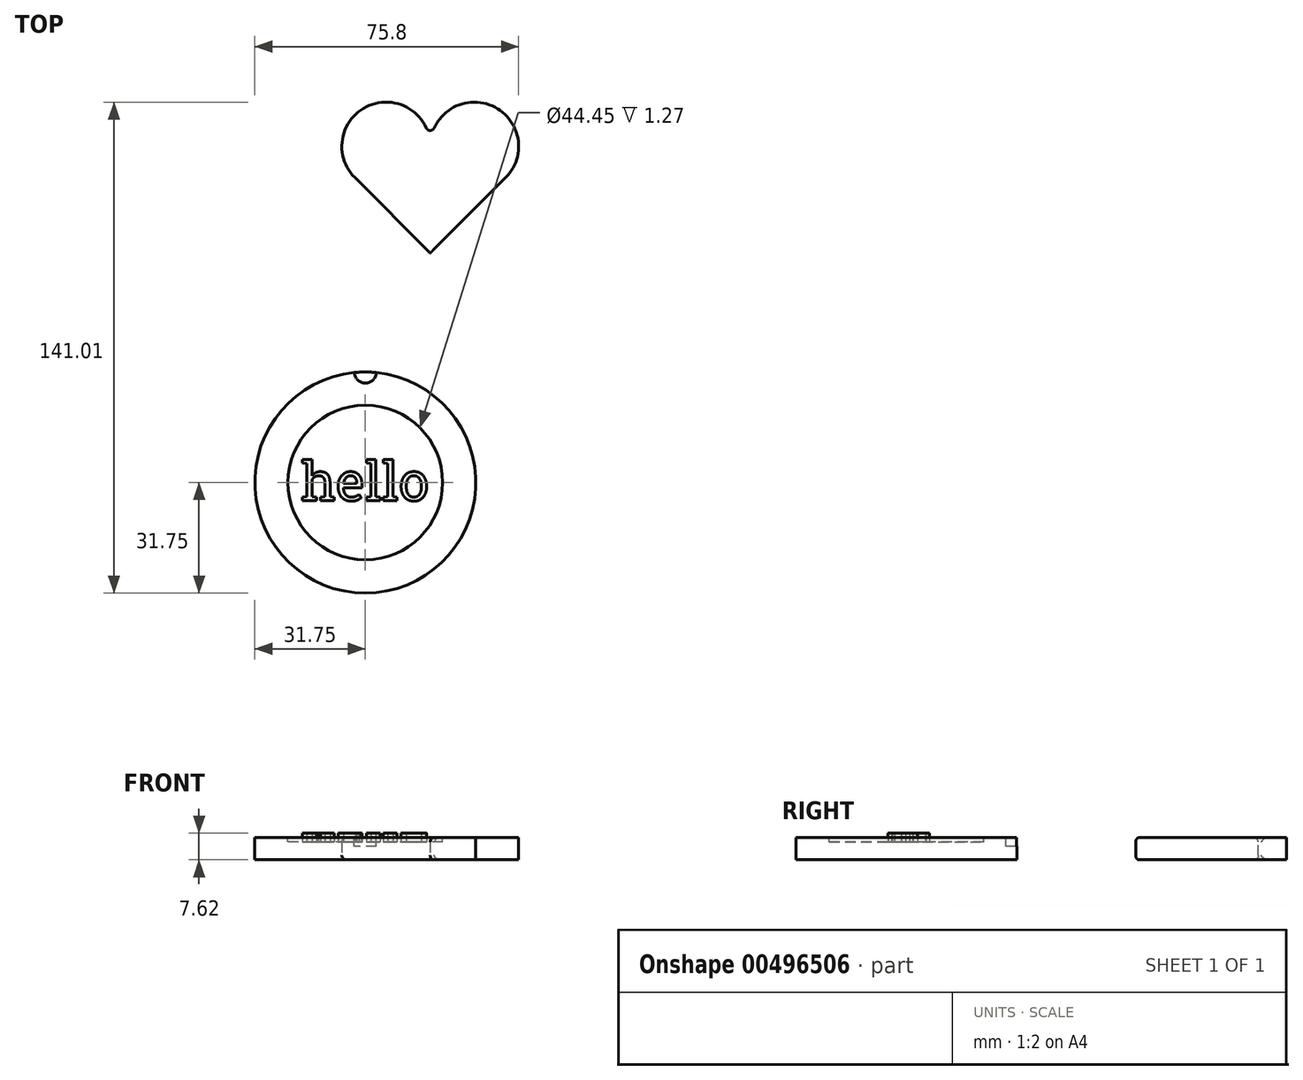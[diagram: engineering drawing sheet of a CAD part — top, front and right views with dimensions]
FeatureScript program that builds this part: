
annotation { "Feature Type Name" : "Feature", "Feature Type Description" : "" }
export const myFeature = defineFeature(function(context is Context, id is Id, definition is map)
    precondition{}
    {
        {
            var Q0;
            Q0=qCreatedBy(makeId("Top.planeOp"),FACE);
            var sketch = newSketch(context, id + "F0", { "sketchPlane" : qUnion([Q0])});
            skCircle(sketch, "E0", {"center": v(0, 0) * mm, "radius": 31.75 * mm});
            skSolve(sketch);
        }
        {
            var Q0;
            Q0 = qSketchRegion(id + "F0", true);
            extrude(context, id + "F1", {"entities" : qUnion([Q0]), "depth" : 6.35 * mm});
        }
        {
            var Q0;
            Q0=makeQuery(id+"F1.opExtrude","CAP_FACE",FACE,{"disambiguationData":[OSD([sQuery(id+"F0.wireOp",EDGE,"E0")])],"isStart":false});
            var sketch = newSketch(context, id + "F2", { "sketchPlane" : qUnion([Q0])});
            skCircle(sketch, "E1", {"center": v(0, 0) * mm, "radius": 22.23 * mm});
            skSolve(sketch);
        }
        {
            var Q0;
            Q0=makeQuery(id+"F2.imprint","IMPRINT",FACE,{"disambiguationData":[TD([[makeQuery(id+"F2.imprint","IMPRINT",EDGE,{"derivedFrom":sQuery(id+"F2.wireOp",EDGE,"E1")}),1.0]])]});
            extrude(context, id + "F3", {"entities" : qUnion([Q0]), "operationType" : NewBodyOperationType.REMOVE, "oppositeDirection" : true, "depth" : 1.27 * mm});
        }
        {
            var Q0;
            Q0=makeQuery(id+"F3.boolean.opBoolean","COPY",FACE,{"derivedFrom":makeQuery(id+"F3.opExtrude","CAP_FACE",FACE,{"disambiguationData":[OSD([sQuery(id+"F2.wireOp",EDGE,"E1")])],"isStart":false})});
            var sketch = newSketch(context, id + "F4", { "sketchPlane" : qUnion([Q0])});
            skText(sketch, "E2", { "text": "hello", "fontName": "RobotoSlab-Regular.ttf"});
            const initialGuessF4  = {"E2": [-0.0185, -0.0052, 1, 0, 0.01116]};
            skSetInitialGuess(sketch, initialGuessF4);
            skSolve(sketch);
        }
        {
            var Q0;
            Q0 = qSketchRegion(id + "F4", true);
            extrude(context, id + "F5", {"entities" : qUnion([Q0]), "operationType" : NewBodyOperationType.ADD, "depth" : 2.54 * mm});
        }
        {
            var Q0;
            Q0=makeQuery(id+"F1.opExtrude","CAP_FACE",FACE,{"disambiguationData":[OSD([sQuery(id+"F0.wireOp",EDGE,"E0")])],"isStart":false});
            var sketch = newSketch(context, id + "F6", { "sketchPlane" : qUnion([Q0])});
            skCircle(sketch, "E3", {"center": v(0, 31.75) * mm, "radius": 3.18 * mm});
            skSolve(sketch);
        }
        {
            var Q0;
            Q0 = qSketchRegion(id + "F6", true);
            extrude(context, id + "F7", {"entities" : qUnion([Q0]), "operationType" : NewBodyOperationType.REMOVE, "oppositeDirection" : true, "depth" : 2.54 * mm});
        }
        {
            var Q0;
            Q0=qCreatedBy(makeId("Top.planeOp"),FACE);
            var sketch = newSketch(context, id + "F8", { "sketchPlane" : qUnion([Q0])});
            skCircle(sketch, "E4", {"center": v(5.95, 96.56) * mm, "radius": 12.7 * mm});
            skCircle(sketch, "E5", {"center": v(31.35, 96.56) * mm, "radius": 12.7 * mm});
            skLineSegment(sketch, "E6", {"start": v(18.65, 96.56) * mm, "end": v(18.65, 59.54) * mm, "construction": true});
            skLineSegment(sketch, "E7", {"start": v(-3.03, 87.58) * mm, "end": v(18.65, 65.9) * mm});
            skLineSegment(sketch, "E8", {"start": v(18.65, 65.9) * mm, "end": v(40.33, 87.58) * mm});
            skLineSegment(sketch, "E9", {"start": v(-12.41, 87.58) * mm, "end": v(51.06, 87.58) * mm, "construction": true});
            skSolve(sketch);
        }
        {
            var Q0;
            Q0 = qSketchRegion(id + "F8", true);
            extrude(context, id + "F9", {"entities" : qUnion([Q0]), "depth" : 6.35 * mm});
        }
        {
            var Q0;
            Q0=makeQuery(id+"F9.opExtrude","SWEPT_FACE",FACE,{"disambiguationData":[OSD([sQuery(id+"F8.wireOp",EDGE,"E4")])]});
            fillet(context, id + "F10", {"entities" : qUnion([Q0]), "radius" : 1.27 * mm, "tangentPropagation" : true, "allowEdgeOverflow" : false});
        }
    });
